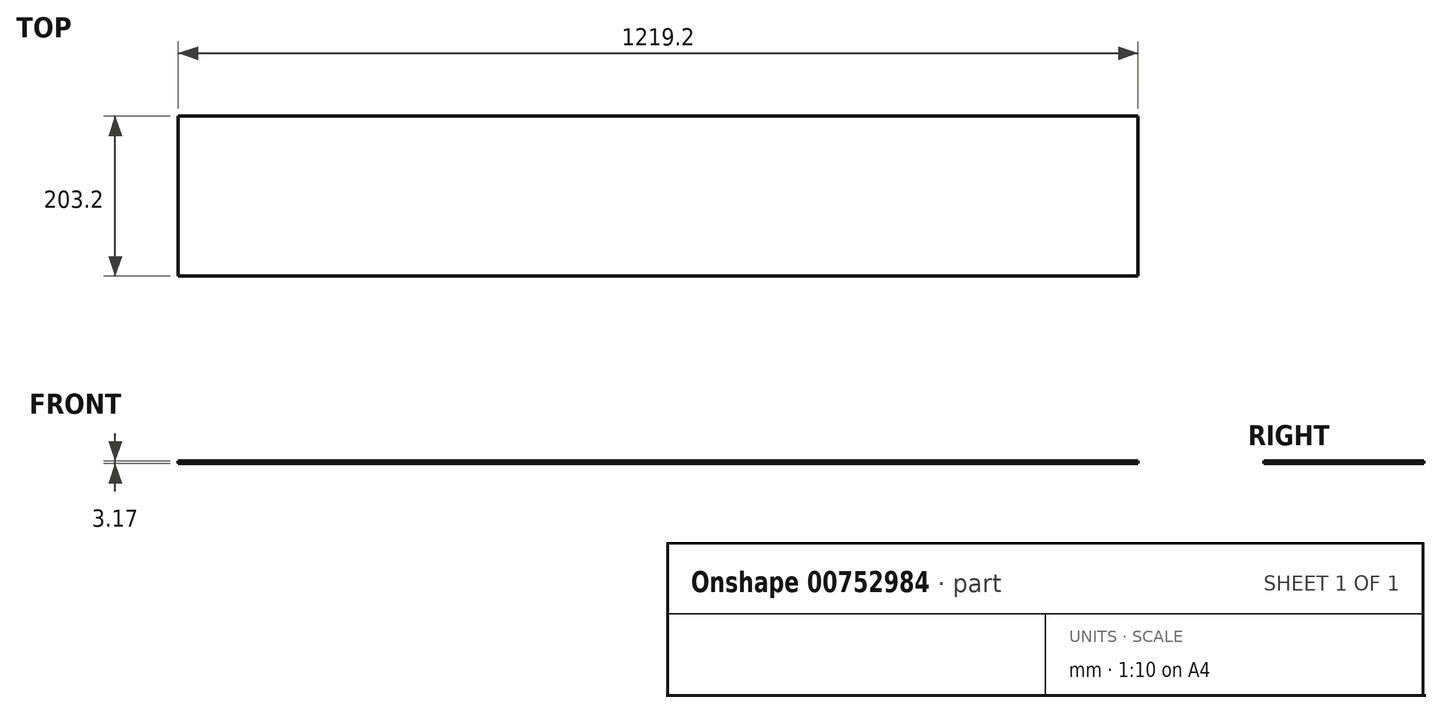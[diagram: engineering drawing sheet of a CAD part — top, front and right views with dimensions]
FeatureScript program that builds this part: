
annotation { "Feature Type Name" : "Feature", "Feature Type Description" : "" }
export const myFeature = defineFeature(function(context is Context, id is Id, definition is map)
    precondition{}
    {
        {
            var Q0;
            Q0=qCreatedBy(makeId("Top.planeOp"),FACE);
            var sketch = newSketch(context, id + "F0", { "sketchPlane" : qUnion([Q0])});
            skLineSegment(sketch, "E0.bottom", {"start": v(609.6, 101.6) * mm, "end": v(-609.6, 101.6) * mm});
            skLineSegment(sketch, "E0.top", {"start": v(609.6, -101.6) * mm, "end": v(-609.6, -101.6) * mm});
            skLineSegment(sketch, "E0.left", {"start": v(609.6, 101.6) * mm, "end": v(609.6, -101.6) * mm});
            skLineSegment(sketch, "E0.right", {"start": v(-609.6, 101.6) * mm, "end": v(-609.6, -101.6) * mm});
            skPoint(sketch, "E0.middle", {"position": v(0, 0) * mm});
            skSolve(sketch);
        }
        {
            var Q0;
            Q0 = qSketchRegion(id + "F0", true);
            extrude(context, id + "F1", {"entities" : qUnion([Q0]), "depth" : 3.17 * mm, "offsetDistance" : 25.4 * mm});
        }
    });
